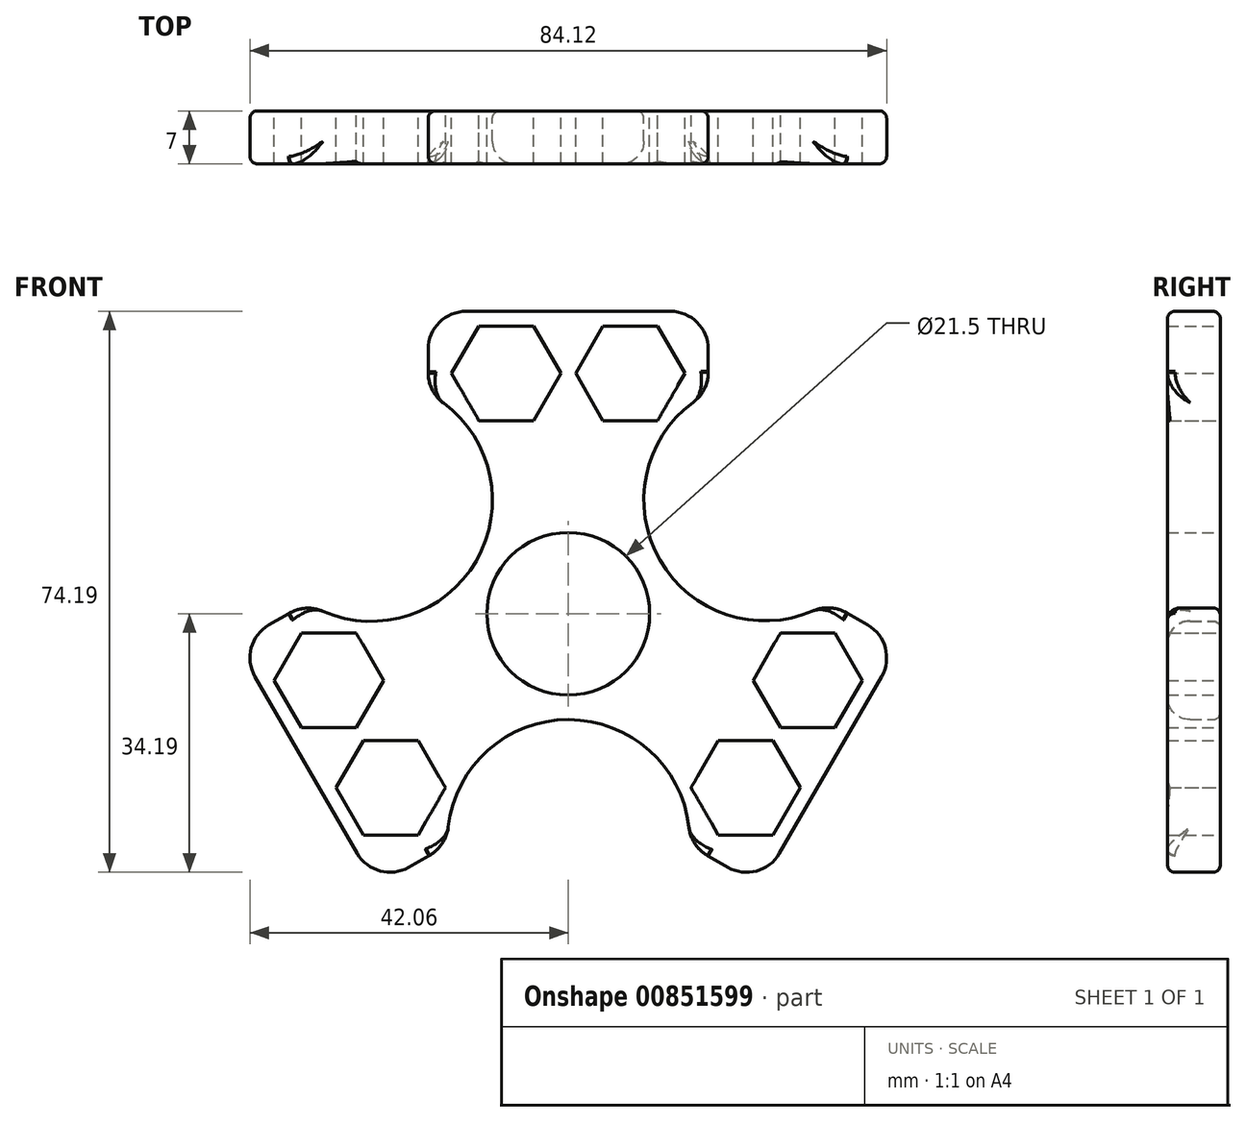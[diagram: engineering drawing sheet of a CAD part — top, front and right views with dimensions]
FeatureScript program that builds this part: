
annotation { "Feature Type Name" : "Feature", "Feature Type Description" : "" }
export const myFeature = defineFeature(function(context is Context, id is Id, definition is map)
    precondition{}
    {
        {
            var Q0;
            Q0=qCreatedBy(makeId("Front.planeOp"),FACE);
            var sketch = newSketch(context, id + "F0", { "sketchPlane" : qUnion([Q0])});
            skLineSegment(sketch, "E0", {"start": v(-11.55, 20) * mm, "end": v(-23.1, 0) * mm});
            skLineSegment(sketch, "E1", {"start": v(-11.55, -20) * mm, "end": v(11.55, -20) * mm});
            skLineSegment(sketch, "E2", {"start": v(23.1, 0) * mm, "end": v(11.55, 20) * mm});
            skLineSegment(sketch, "E3", {"start": v(-34.64, -20) * mm, "end": v(17.32, 10) * mm, "construction": true});
            skLineSegment(sketch, "E4", {"start": v(-17.32, 10) * mm, "end": v(34.64, -20) * mm, "construction": true});
            skLineSegment(sketch, "E5", {"start": v(0, -20) * mm, "end": v(0, 40) * mm, "construction": true});
            skLineSegment(sketch, "E6.bottom", {"start": v(18.5, 40) * mm, "end": v(-18.5, 40) * mm});
            skLineSegment(sketch, "E6.top", {"start": v(18.5, 20) * mm, "end": v(11.55, 20) * mm});
            skLineSegment(sketch, "E6.left", {"start": v(18.5, 40) * mm, "end": v(18.5, 20) * mm});
            skLineSegment(sketch, "E6.right", {"start": v(-18.5, 40) * mm, "end": v(-18.5, 20) * mm});
            skLineSegment(sketch, "E7", {"start": v(-43.9, -3.98) * mm, "end": v(-25.4, -36.02) * mm});
            skLineSegment(sketch, "E8", {"start": v(-25.4, -36.02) * mm, "end": v(-8.07, -26.02) * mm});
            skLineSegment(sketch, "E9", {"start": v(-8.07, -26.02) * mm, "end": v(-11.55, -20) * mm});
            skLineSegment(sketch, "E10", {"start": v(-26.57, 6.02) * mm, "end": v(-43.9, -3.98) * mm});
            skLineSegment(sketch, "E11", {"start": v(43.9, -3.98) * mm, "end": v(25.4, -36.02) * mm});
            skLineSegment(sketch, "E12", {"start": v(43.9, -3.98) * mm, "end": v(26.57, 6.02) * mm});
            skLineSegment(sketch, "E13", {"start": v(26.57, 6.02) * mm, "end": v(23.1, 0) * mm});
            skLineSegment(sketch, "E14", {"start": v(8.07, -26.02) * mm, "end": v(25.4, -36.02) * mm});
            skPoint(sketch, "E15.startSnap0", {"position": v(-35.23, 1.02) * mm});
            skLineSegment(sketch, "E16.trimOffspring", {"start": v(-23.1, 0) * mm, "end": v(-26.57, 6.02) * mm});
            skLineSegment(sketch, "E17.trimOffspring", {"start": v(11.55, -20) * mm, "end": v(8.07, -26.02) * mm});
            skLineSegment(sketch, "E18.trimOffspring", {"start": v(-11.55, 20) * mm, "end": v(-18.5, 20) * mm});
            skSolve(sketch);
        }
        {
            var Q0;
            Q0=makeQuery(id+"F0.imprint","IMPRINT",FACE,{"disambiguationData":[TD([[makeQuery(id+"F0.imprint","IMPRINT",EDGE,{"derivedFrom":sQuery(id+"F0.wireOp",EDGE,"E0")}),1.0]])]});
            extrude(context, id + "F1", {"entities" : qUnion([Q0]), "depth" : 7 * mm, "offsetDistance" : 25 * mm});
        }
        {
            var Q0;
            Q0=makeQuery(id+"F1.opExtrude","CAP_FACE",FACE,{"disambiguationData":[OSD([sQuery(id+"F0.wireOp",EDGE,"E0"),sQuery(id+"F0.wireOp",EDGE,"E1"),sQuery(id+"F0.wireOp",EDGE,"E2"),sQuery(id+"F0.wireOp",EDGE,"E6.bottom"),sQuery(id+"F0.wireOp",EDGE,"E6.top"),sQuery(id+"F0.wireOp",EDGE,"E6.left"),sQuery(id+"F0.wireOp",EDGE,"E6.right"),sQuery(id+"F0.wireOp",EDGE,"E7"),sQuery(id+"F0.wireOp",EDGE,"E8"),sQuery(id+"F0.wireOp",EDGE,"E9"),sQuery(id+"F0.wireOp",EDGE,"E10"),sQuery(id+"F0.wireOp",EDGE,"E11"),sQuery(id+"F0.wireOp",EDGE,"E12"),sQuery(id+"F0.wireOp",EDGE,"E13"),sQuery(id+"F0.wireOp",EDGE,"E14"),sQuery(id+"F0.wireOp",EDGE,"E16.trimOffspring"),sQuery(id+"F0.wireOp",EDGE,"E17.trimOffspring"),sQuery(id+"F0.wireOp",EDGE,"E18.trimOffspring")])],"isStart":true});
            var sketch = newSketch(context, id + "F2", { "sketchPlane" : qUnion([Q0])});
            skPoint(sketch, "E19.0", {"position": v(18.5, 30) * mm});
            skPoint(sketch, "E20.0", {"position": v(-18.5, 30) * mm});
            skPoint(sketch, "E21.0", {"position": v(-35.23, 1.02) * mm});
            skPoint(sketch, "E22.0", {"position": v(-16.73, -31.02) * mm});
            skPoint(sketch, "E23.0", {"position": v(16.73, -31.02) * mm});
            skPoint(sketch, "E24.0", {"position": v(35.23, 1.02) * mm});
            skLineSegment(sketch, "E25", {"start": v(-25.98, 15.07) * mm, "end": v(-9.98, 15.05) * mm});
            skLineSegment(sketch, "E26", {"start": v(-0.04, -30) * mm, "end": v(7.98, -16.15) * mm});
            skLineSegment(sketch, "E27", {"start": v(-0.04, -30) * mm, "end": v(-8.02, -16.13) * mm});
            skCircle(sketch, "E28", {"center": v(-25.98, 15.07) * mm, "radius": 16 * mm});
            skCircle(sketch, "E29", {"center": v(26.02, 15) * mm, "radius": 16 * mm});
            skCircle(sketch, "E30", {"center": v(-0.04, -30) * mm, "radius": 16 * mm});
            skLineSegment(sketch, "E31.trimOffspring", {"start": v(10.02, 15.02) * mm, "end": v(26.02, 15) * mm});
            skLineSegment(sketch, "E32.trimOffspring", {"start": v(-18, 1.2) * mm, "end": v(-25.98, 15.07) * mm});
            skLineSegment(sketch, "E33.trimOffspring", {"start": v(18, 1.15) * mm, "end": v(26.02, 15) * mm});
            skSolve(sketch);
        }
        {
            var Q0;
            Q0 = qSketchRegion(id + "F2", true);
            extrude(context, id + "F3", {"entities" : qUnion([Q0]), "operationType" : NewBodyOperationType.REMOVE, "oppositeDirection" : true, "depth" : 25 * mm, "offsetDistance" : 25 * mm});
        }
        {
            var Q0;
            Q0 = qSketchRegion(id + "F2", true);
            extrude(context, id + "F4", {"entities" : qUnion([Q0]), "operationType" : NewBodyOperationType.REMOVE, "oppositeDirection" : true, "depth" : 25 * mm, "offsetDistance" : 25 * mm});
        }
        {
            var Q0;
            Q0=makeQuery(id+"F3.boolean.opBoolean","INTERSECT",EDGE,{"derivedFrom":[makeQuery(id+"F1.opExtrude","SWEPT_FACE",FACE,{"disambiguationData":[OSD([sQuery(id+"F0.wireOp",EDGE,"E6.left")])]}),makeQuery(id+"F3.opExtrude","SWEPT_FACE",FACE,{"disambiguationData":[OSD([sQuery(id+"F2.wireOp",EDGE,"E28")])]})]});
            var Q1;
            Q1=makeQuery(id+"F3.boolean.opBoolean","INTERSECT",EDGE,{"derivedFrom":[makeQuery(id+"F1.opExtrude","SWEPT_FACE",FACE,{"disambiguationData":[OSD([sQuery(id+"F0.wireOp",EDGE,"E6.right")])]}),makeQuery(id+"F3.opExtrude","SWEPT_FACE",FACE,{"disambiguationData":[OSD([sQuery(id+"F2.wireOp",EDGE,"E29")])]})]});
            var Q2;
            Q2=makeQuery(id+"F3.boolean.opBoolean","INTERSECT",EDGE,{"derivedFrom":[makeQuery(id+"F1.opExtrude","SWEPT_FACE",FACE,{"disambiguationData":[OSD([sQuery(id+"F0.wireOp",EDGE,"E10")])]}),makeQuery(id+"F3.opExtrude","SWEPT_FACE",FACE,{"disambiguationData":[OSD([sQuery(id+"F2.wireOp",EDGE,"E29")])]})]});
            var Q3;
            Q3=makeQuery(id+"F3.boolean.opBoolean","INTERSECT",EDGE,{"derivedFrom":[makeQuery(id+"F1.opExtrude","SWEPT_FACE",FACE,{"disambiguationData":[OSD([sQuery(id+"F0.wireOp",EDGE,"E8")])]}),makeQuery(id+"F3.opExtrude","SWEPT_FACE",FACE,{"disambiguationData":[OSD([sQuery(id+"F2.wireOp",EDGE,"E30")])]})]});
            var Q4;
            Q4=makeQuery(id+"F3.boolean.opBoolean","INTERSECT",EDGE,{"derivedFrom":[makeQuery(id+"F1.opExtrude","SWEPT_FACE",FACE,{"disambiguationData":[OSD([sQuery(id+"F0.wireOp",EDGE,"E12")])]}),makeQuery(id+"F3.opExtrude","SWEPT_FACE",FACE,{"disambiguationData":[OSD([sQuery(id+"F2.wireOp",EDGE,"E28")])]})]});
            var Q5;
            Q5=makeQuery(id+"F3.boolean.opBoolean","INTERSECT",EDGE,{"derivedFrom":[makeQuery(id+"F1.opExtrude","SWEPT_FACE",FACE,{"disambiguationData":[OSD([sQuery(id+"F0.wireOp",EDGE,"E14")])]}),makeQuery(id+"F3.opExtrude","SWEPT_FACE",FACE,{"disambiguationData":[OSD([sQuery(id+"F2.wireOp",EDGE,"E30")])]})]});
            fillet(context, id + "F5", {"entities" : qUnion([Q0, Q1, Q2, Q3, Q4, Q5]), "radius" : 5 * mm, "tangentPropagation" : true, "allowEdgeOverflow" : false});
        }
        {
            var Q0;
            Q0=makeQuery(id+"F1.opExtrude","SWEPT_EDGE",EDGE,{"disambiguationData":[OSD([sQuery(id+"F0.wireOp",EDGE,"E7"),sQuery(id+"F0.wireOp",EDGE,"E8")])]});
            var Q1;
            Q1=makeQuery(id+"F1.opExtrude","SWEPT_EDGE",EDGE,{"disambiguationData":[OSD([sQuery(id+"F0.wireOp",EDGE,"E7"),sQuery(id+"F0.wireOp",EDGE,"E10")])]});
            var Q2;
            Q2=makeQuery(id+"F1.opExtrude","SWEPT_EDGE",EDGE,{"disambiguationData":[OSD([sQuery(id+"F0.wireOp",EDGE,"E6.bottom"),sQuery(id+"F0.wireOp",EDGE,"E6.right")])]});
            var Q3;
            Q3=makeQuery(id+"F1.opExtrude","SWEPT_EDGE",EDGE,{"disambiguationData":[OSD([sQuery(id+"F0.wireOp",EDGE,"E6.bottom"),sQuery(id+"F0.wireOp",EDGE,"E6.left")])]});
            var Q4;
            Q4=makeQuery(id+"F1.opExtrude","SWEPT_EDGE",EDGE,{"disambiguationData":[OSD([sQuery(id+"F0.wireOp",EDGE,"E11"),sQuery(id+"F0.wireOp",EDGE,"E12")])]});
            var Q5;
            Q5=makeQuery(id+"F1.opExtrude","SWEPT_EDGE",EDGE,{"disambiguationData":[OSD([sQuery(id+"F0.wireOp",EDGE,"E11"),sQuery(id+"F0.wireOp",EDGE,"E14")])]});
            fillet(context, id + "F6", {"entities" : qUnion([Q0, Q1, Q2, Q3, Q4, Q5]), "radius" : 5 * mm, "tangentPropagation" : true, "allowEdgeOverflow" : false});
        }
        {
            var Q0;
            Q0=makeQuery(id+"F1.opExtrude","CAP_FACE",FACE,{"disambiguationData":[OSD([sQuery(id+"F0.wireOp",EDGE,"E0"),sQuery(id+"F0.wireOp",EDGE,"E1"),sQuery(id+"F0.wireOp",EDGE,"E2"),sQuery(id+"F0.wireOp",EDGE,"E6.bottom"),sQuery(id+"F0.wireOp",EDGE,"E6.top"),sQuery(id+"F0.wireOp",EDGE,"E6.left"),sQuery(id+"F0.wireOp",EDGE,"E6.right"),sQuery(id+"F0.wireOp",EDGE,"E7"),sQuery(id+"F0.wireOp",EDGE,"E8"),sQuery(id+"F0.wireOp",EDGE,"E9"),sQuery(id+"F0.wireOp",EDGE,"E10"),sQuery(id+"F0.wireOp",EDGE,"E11"),sQuery(id+"F0.wireOp",EDGE,"E12"),sQuery(id+"F0.wireOp",EDGE,"E13"),sQuery(id+"F0.wireOp",EDGE,"E14"),sQuery(id+"F0.wireOp",EDGE,"E16.trimOffspring"),sQuery(id+"F0.wireOp",EDGE,"E17.trimOffspring"),sQuery(id+"F0.wireOp",EDGE,"E18.trimOffspring")])],"isStart":true});
            var sketch = newSketch(context, id + "F7", { "sketchPlane" : qUnion([Q0])});
            skLineSegment(sketch, "E34", {"start": v(0, 0) * mm, "end": v(34.64, -20) * mm, "construction": true});
            skLineSegment(sketch, "E35", {"start": v(-34.64, -20) * mm, "end": v(0, 0) * mm, "construction": true});
            skLineSegment(sketch, "E36", {"start": v(0, 40) * mm, "end": v(0, 0) * mm, "construction": true});
            skCircle(sketch, "E37.cCircle", {"center": v(31.64, -8.8) * mm, "radius": 6.25 * mm, "construction": true});
            skLineSegment(sketch, "E37.0", {"start": v(35.25, -2.55) * mm, "end": v(38.86, -8.8) * mm});
            skLineSegment(sketch, "E37.1", {"start": v(38.86, -8.8) * mm, "end": v(35.25, -15.05) * mm});
            skLineSegment(sketch, "E37.2", {"start": v(35.25, -15.05) * mm, "end": v(28.03, -15.05) * mm});
            skLineSegment(sketch, "E37.3", {"start": v(28.03, -15.05) * mm, "end": v(24.42, -8.8) * mm});
            skLineSegment(sketch, "E37.4", {"start": v(24.42, -8.8) * mm, "end": v(28.03, -2.55) * mm});
            skLineSegment(sketch, "E37.5", {"start": v(28.03, -2.55) * mm, "end": v(35.25, -2.55) * mm});
            skPoint(sketch, "E37.0.midPoint", {"position": v(37.05, -5.67) * mm});
            skCircle(sketch, "E38.cCircle", {"center": v(23.44, -23) * mm, "radius": 6.25 * mm, "construction": true});
            skLineSegment(sketch, "E38.0", {"start": v(27.05, -29.25) * mm, "end": v(19.83, -29.25) * mm});
            skLineSegment(sketch, "E38.1", {"start": v(19.83, -29.25) * mm, "end": v(16.22, -23) * mm});
            skLineSegment(sketch, "E38.2", {"start": v(16.22, -23) * mm, "end": v(19.83, -16.75) * mm});
            skLineSegment(sketch, "E38.3", {"start": v(19.83, -16.75) * mm, "end": v(27.05, -16.75) * mm});
            skLineSegment(sketch, "E38.4", {"start": v(27.05, -16.75) * mm, "end": v(30.66, -23) * mm});
            skLineSegment(sketch, "E38.5", {"start": v(30.66, -23) * mm, "end": v(27.05, -29.25) * mm});
            skPoint(sketch, "E38.0.midPoint", {"position": v(23.44, -29.25) * mm});
            skLineSegment(sketch, "E39.1.0", {"start": v(-4.6, 25.55) * mm, "end": v(-11.8, 25.55) * mm});
            skCircle(sketch, "E39.1.1", {"center": v(-8.2, 31.8) * mm, "radius": 6.25 * mm, "construction": true});
            skLineSegment(sketch, "E39.1.2", {"start": v(-11.8, 25.55) * mm, "end": v(-15.42, 31.8) * mm});
            skLineSegment(sketch, "E39.1.3", {"start": v(-15.42, 31.8) * mm, "end": v(-11.8, 38.05) * mm});
            skLineSegment(sketch, "E39.1.4", {"start": v(-11.8, 38.05) * mm, "end": v(-4.6, 38.05) * mm});
            skLineSegment(sketch, "E39.1.5", {"start": v(-4.6, 38.05) * mm, "end": v(-0.98, 31.8) * mm});
            skLineSegment(sketch, "E39.1.6", {"start": v(-0.98, 31.8) * mm, "end": v(-4.6, 25.55) * mm});
            skLineSegment(sketch, "E39.1.7", {"start": v(4.6, 25.55) * mm, "end": v(0.98, 31.8) * mm});
            skLineSegment(sketch, "E39.1.8", {"start": v(11.8, 25.55) * mm, "end": v(4.6, 25.55) * mm});
            skCircle(sketch, "E39.1.9", {"center": v(8.2, 31.8) * mm, "radius": 6.25 * mm, "construction": true});
            skLineSegment(sketch, "E39.1.10", {"start": v(0.98, 31.8) * mm, "end": v(4.6, 38.05) * mm});
            skLineSegment(sketch, "E39.1.11", {"start": v(4.6, 38.05) * mm, "end": v(11.8, 38.05) * mm});
            skLineSegment(sketch, "E39.1.12", {"start": v(11.8, 38.05) * mm, "end": v(15.42, 31.8) * mm});
            skLineSegment(sketch, "E39.1.13", {"start": v(15.42, 31.8) * mm, "end": v(11.8, 25.55) * mm});
            skLineSegment(sketch, "E39.2.0", {"start": v(-19.83, -16.75) * mm, "end": v(-16.22, -23) * mm});
            skCircle(sketch, "E39.2.1", {"center": v(-23.44, -23) * mm, "radius": 6.25 * mm, "construction": true});
            skLineSegment(sketch, "E39.2.2", {"start": v(-16.22, -23) * mm, "end": v(-19.83, -29.25) * mm});
            skLineSegment(sketch, "E39.2.3", {"start": v(-19.83, -29.25) * mm, "end": v(-27.05, -29.25) * mm});
            skLineSegment(sketch, "E39.2.4", {"start": v(-27.05, -29.25) * mm, "end": v(-30.66, -23) * mm});
            skLineSegment(sketch, "E39.2.5", {"start": v(-30.66, -23) * mm, "end": v(-27.05, -16.75) * mm});
            skLineSegment(sketch, "E39.2.6", {"start": v(-27.05, -16.75) * mm, "end": v(-19.83, -16.75) * mm});
            skLineSegment(sketch, "E39.2.7", {"start": v(-24.42, -8.8) * mm, "end": v(-28.03, -15.05) * mm});
            skLineSegment(sketch, "E39.2.8", {"start": v(-28.03, -2.55) * mm, "end": v(-24.42, -8.8) * mm});
            skCircle(sketch, "E39.2.9", {"center": v(-31.64, -8.8) * mm, "radius": 6.25 * mm, "construction": true});
            skLineSegment(sketch, "E39.2.10", {"start": v(-28.03, -15.05) * mm, "end": v(-35.25, -15.05) * mm});
            skLineSegment(sketch, "E39.2.11", {"start": v(-35.25, -15.05) * mm, "end": v(-38.86, -8.8) * mm});
            skLineSegment(sketch, "E39.2.12", {"start": v(-38.86, -8.8) * mm, "end": v(-35.25, -2.55) * mm});
            skLineSegment(sketch, "E39.2.13", {"start": v(-35.25, -2.55) * mm, "end": v(-28.03, -2.55) * mm});
            skPoint(sketch, "E39.center", {"position": v(0, 0) * mm});
            skSolve(sketch);
        }
        {
            var Q0;
            Q0 = qSketchRegion(id + "F7", true);
            extrude(context, id + "F8", {"entities" : qUnion([Q0]), "operationType" : NewBodyOperationType.REMOVE, "oppositeDirection" : true, "depth" : 25 * mm, "offsetDistance" : 25 * mm});
        }
        {
            var Q0;
            Q0=makeQuery(id+"F3.boolean.opBoolean","INTERSECT",EDGE,{"derivedFrom":[makeQuery(id+"F1.opExtrude","CAP_FACE",FACE,{"disambiguationData":[OSD([sQuery(id+"F0.wireOp",EDGE,"E0"),sQuery(id+"F0.wireOp",EDGE,"E1"),sQuery(id+"F0.wireOp",EDGE,"E2"),sQuery(id+"F0.wireOp",EDGE,"E6.bottom"),sQuery(id+"F0.wireOp",EDGE,"E6.top"),sQuery(id+"F0.wireOp",EDGE,"E6.left"),sQuery(id+"F0.wireOp",EDGE,"E6.right"),sQuery(id+"F0.wireOp",EDGE,"E7"),sQuery(id+"F0.wireOp",EDGE,"E8"),sQuery(id+"F0.wireOp",EDGE,"E9"),sQuery(id+"F0.wireOp",EDGE,"E10"),sQuery(id+"F0.wireOp",EDGE,"E11"),sQuery(id+"F0.wireOp",EDGE,"E12"),sQuery(id+"F0.wireOp",EDGE,"E13"),sQuery(id+"F0.wireOp",EDGE,"E14"),sQuery(id+"F0.wireOp",EDGE,"E16.trimOffspring"),sQuery(id+"F0.wireOp",EDGE,"E17.trimOffspring"),sQuery(id+"F0.wireOp",EDGE,"E18.trimOffspring")])],"isStart":false}),makeQuery(id+"F3.opExtrude","SWEPT_FACE",FACE,{"disambiguationData":[OSD([sQuery(id+"F2.wireOp",EDGE,"E29")])]})]});
            var Q1;
            Q1=makeQuery(id+"F3.boolean.opBoolean","COPY",EDGE,{"derivedFrom":makeQuery(id+"F3.opExtrude","CAP_EDGE",EDGE,{"disambiguationData":[OSD([sQuery(id+"F2.wireOp",EDGE,"E29")])],"isStart":true})});
            var Q2;
            Q2=makeQuery(id+"F3.boolean.opBoolean","INTERSECT",EDGE,{"derivedFrom":[makeQuery(id+"F1.opExtrude","CAP_FACE",FACE,{"disambiguationData":[OSD([sQuery(id+"F0.wireOp",EDGE,"E0"),sQuery(id+"F0.wireOp",EDGE,"E1"),sQuery(id+"F0.wireOp",EDGE,"E2"),sQuery(id+"F0.wireOp",EDGE,"E6.bottom"),sQuery(id+"F0.wireOp",EDGE,"E6.top"),sQuery(id+"F0.wireOp",EDGE,"E6.left"),sQuery(id+"F0.wireOp",EDGE,"E6.right"),sQuery(id+"F0.wireOp",EDGE,"E7"),sQuery(id+"F0.wireOp",EDGE,"E8"),sQuery(id+"F0.wireOp",EDGE,"E9"),sQuery(id+"F0.wireOp",EDGE,"E10"),sQuery(id+"F0.wireOp",EDGE,"E11"),sQuery(id+"F0.wireOp",EDGE,"E12"),sQuery(id+"F0.wireOp",EDGE,"E13"),sQuery(id+"F0.wireOp",EDGE,"E14"),sQuery(id+"F0.wireOp",EDGE,"E16.trimOffspring"),sQuery(id+"F0.wireOp",EDGE,"E17.trimOffspring"),sQuery(id+"F0.wireOp",EDGE,"E18.trimOffspring")])],"isStart":false}),makeQuery(id+"F3.opExtrude","SWEPT_FACE",FACE,{"disambiguationData":[OSD([sQuery(id+"F2.wireOp",EDGE,"E30")])]})]});
            var Q3;
            Q3=makeQuery(id+"F3.boolean.opBoolean","INTERSECT",EDGE,{"derivedFrom":[makeQuery(id+"F1.opExtrude","CAP_FACE",FACE,{"disambiguationData":[OSD([sQuery(id+"F0.wireOp",EDGE,"E0"),sQuery(id+"F0.wireOp",EDGE,"E1"),sQuery(id+"F0.wireOp",EDGE,"E2"),sQuery(id+"F0.wireOp",EDGE,"E6.bottom"),sQuery(id+"F0.wireOp",EDGE,"E6.top"),sQuery(id+"F0.wireOp",EDGE,"E6.left"),sQuery(id+"F0.wireOp",EDGE,"E6.right"),sQuery(id+"F0.wireOp",EDGE,"E7"),sQuery(id+"F0.wireOp",EDGE,"E8"),sQuery(id+"F0.wireOp",EDGE,"E9"),sQuery(id+"F0.wireOp",EDGE,"E10"),sQuery(id+"F0.wireOp",EDGE,"E11"),sQuery(id+"F0.wireOp",EDGE,"E12"),sQuery(id+"F0.wireOp",EDGE,"E13"),sQuery(id+"F0.wireOp",EDGE,"E14"),sQuery(id+"F0.wireOp",EDGE,"E16.trimOffspring"),sQuery(id+"F0.wireOp",EDGE,"E17.trimOffspring"),sQuery(id+"F0.wireOp",EDGE,"E18.trimOffspring")])],"isStart":false}),makeQuery(id+"F3.opExtrude","SWEPT_FACE",FACE,{"disambiguationData":[OSD([sQuery(id+"F2.wireOp",EDGE,"E28")])]})]});
            var Q4;
            Q4=makeQuery(id+"F3.boolean.opBoolean","COPY",EDGE,{"derivedFrom":makeQuery(id+"F3.opExtrude","CAP_EDGE",EDGE,{"disambiguationData":[OSD([sQuery(id+"F2.wireOp",EDGE,"E28")])],"isStart":true})});
            var Q5;
            Q5=makeQuery(id+"F3.boolean.opBoolean","COPY",EDGE,{"derivedFrom":makeQuery(id+"F3.opExtrude","CAP_EDGE",EDGE,{"disambiguationData":[OSD([sQuery(id+"F2.wireOp",EDGE,"E30")])],"isStart":true})});
            fillet(context, id + "F9", {"entities" : qUnion([Q0, Q1, Q2, Q3, Q4, Q5]), "radius" : 3 * mm, "allowEdgeOverflow" : false});
        }
        {
            var Q0;
            Q0=makeQuery(id+"F1.opExtrude","CAP_FACE",FACE,{"disambiguationData":[OSD([sQuery(id+"F0.wireOp",EDGE,"E0"),sQuery(id+"F0.wireOp",EDGE,"E1"),sQuery(id+"F0.wireOp",EDGE,"E2"),sQuery(id+"F0.wireOp",EDGE,"E6.bottom"),sQuery(id+"F0.wireOp",EDGE,"E6.top"),sQuery(id+"F0.wireOp",EDGE,"E6.left"),sQuery(id+"F0.wireOp",EDGE,"E6.right"),sQuery(id+"F0.wireOp",EDGE,"E7"),sQuery(id+"F0.wireOp",EDGE,"E8"),sQuery(id+"F0.wireOp",EDGE,"E9"),sQuery(id+"F0.wireOp",EDGE,"E10"),sQuery(id+"F0.wireOp",EDGE,"E11"),sQuery(id+"F0.wireOp",EDGE,"E12"),sQuery(id+"F0.wireOp",EDGE,"E13"),sQuery(id+"F0.wireOp",EDGE,"E14"),sQuery(id+"F0.wireOp",EDGE,"E16.trimOffspring"),sQuery(id+"F0.wireOp",EDGE,"E17.trimOffspring"),sQuery(id+"F0.wireOp",EDGE,"E18.trimOffspring")])],"isStart":true});
            var sketch = newSketch(context, id + "F10", { "sketchPlane" : qUnion([Q0])});
            skCircle(sketch, "E40", {"center": v(0, 0) * mm, "radius": 10.75 * mm});
            skSolve(sketch);
        }
        {
            var Q0;
            Q0 = qSketchRegion(id + "F10", true);
            extrude(context, id + "F11", {"entities" : qUnion([Q0]), "operationType" : NewBodyOperationType.REMOVE, "oppositeDirection" : true, "depth" : 25 * mm, "offsetDistance" : 25 * mm});
        }
        {
            var Q0;
            {var subQ0=sQuery(id+"F0.wireOp",EDGE,"E6.left");var subQ1=sQuery(id+"F0.wireOp",EDGE,"E6.bottom");Q0=makeQuery(id+"F6.opFillet","BLEND_EDGE",EDGE,{"blendedFrom":[makeQuery(id+"F1.opExtrude","SWEPT_EDGE",EDGE,{"disambiguationData":[OSD([subQ1,subQ0])]}),makeQuery(id+"F1.opExtrude","CAP_FACE",FACE,{"disambiguationData":[OSD([sQuery(id+"F0.wireOp",EDGE,"E0"),sQuery(id+"F0.wireOp",EDGE,"E1"),sQuery(id+"F0.wireOp",EDGE,"E2"),subQ1,sQuery(id+"F0.wireOp",EDGE,"E6.top"),subQ0,sQuery(id+"F0.wireOp",EDGE,"E6.right"),sQuery(id+"F0.wireOp",EDGE,"E7"),sQuery(id+"F0.wireOp",EDGE,"E8"),sQuery(id+"F0.wireOp",EDGE,"E9"),sQuery(id+"F0.wireOp",EDGE,"E10"),sQuery(id+"F0.wireOp",EDGE,"E11"),sQuery(id+"F0.wireOp",EDGE,"E12"),sQuery(id+"F0.wireOp",EDGE,"E13"),sQuery(id+"F0.wireOp",EDGE,"E14"),sQuery(id+"F0.wireOp",EDGE,"E16.trimOffspring"),sQuery(id+"F0.wireOp",EDGE,"E17.trimOffspring"),sQuery(id+"F0.wireOp",EDGE,"E18.trimOffspring")])],"isStart":false})],"blendedInto":[makeQuery(id+"F1.opExtrude","CAP_FACE",FACE,{"disambiguationData":[OSD([sQuery(id+"F0.wireOp",EDGE,"E0"),sQuery(id+"F0.wireOp",EDGE,"E1"),sQuery(id+"F0.wireOp",EDGE,"E2"),subQ1,sQuery(id+"F0.wireOp",EDGE,"E6.top"),subQ0,sQuery(id+"F0.wireOp",EDGE,"E6.right"),sQuery(id+"F0.wireOp",EDGE,"E7"),sQuery(id+"F0.wireOp",EDGE,"E8"),sQuery(id+"F0.wireOp",EDGE,"E9"),sQuery(id+"F0.wireOp",EDGE,"E10"),sQuery(id+"F0.wireOp",EDGE,"E11"),sQuery(id+"F0.wireOp",EDGE,"E12"),sQuery(id+"F0.wireOp",EDGE,"E13"),sQuery(id+"F0.wireOp",EDGE,"E14"),sQuery(id+"F0.wireOp",EDGE,"E16.trimOffspring"),sQuery(id+"F0.wireOp",EDGE,"E17.trimOffspring"),sQuery(id+"F0.wireOp",EDGE,"E18.trimOffspring")])],"isStart":false})]});}
            var Q1;
            {var subQ0=sQuery(id+"F0.wireOp",EDGE,"E6.right");var subQ1=sQuery(id+"F0.wireOp",EDGE,"E6.bottom");Q1=makeQuery(id+"F6.opFillet","BLEND_EDGE",EDGE,{"blendedFrom":[makeQuery(id+"F1.opExtrude","SWEPT_EDGE",EDGE,{"disambiguationData":[OSD([subQ1,subQ0])]}),makeQuery(id+"F1.opExtrude","CAP_FACE",FACE,{"disambiguationData":[OSD([sQuery(id+"F0.wireOp",EDGE,"E0"),sQuery(id+"F0.wireOp",EDGE,"E1"),sQuery(id+"F0.wireOp",EDGE,"E2"),subQ1,sQuery(id+"F0.wireOp",EDGE,"E6.top"),sQuery(id+"F0.wireOp",EDGE,"E6.left"),subQ0,sQuery(id+"F0.wireOp",EDGE,"E7"),sQuery(id+"F0.wireOp",EDGE,"E8"),sQuery(id+"F0.wireOp",EDGE,"E9"),sQuery(id+"F0.wireOp",EDGE,"E10"),sQuery(id+"F0.wireOp",EDGE,"E11"),sQuery(id+"F0.wireOp",EDGE,"E12"),sQuery(id+"F0.wireOp",EDGE,"E13"),sQuery(id+"F0.wireOp",EDGE,"E14"),sQuery(id+"F0.wireOp",EDGE,"E16.trimOffspring"),sQuery(id+"F0.wireOp",EDGE,"E17.trimOffspring"),sQuery(id+"F0.wireOp",EDGE,"E18.trimOffspring")])],"isStart":true})],"blendedInto":[makeQuery(id+"F1.opExtrude","CAP_FACE",FACE,{"disambiguationData":[OSD([sQuery(id+"F0.wireOp",EDGE,"E0"),sQuery(id+"F0.wireOp",EDGE,"E1"),sQuery(id+"F0.wireOp",EDGE,"E2"),subQ1,sQuery(id+"F0.wireOp",EDGE,"E6.top"),sQuery(id+"F0.wireOp",EDGE,"E6.left"),subQ0,sQuery(id+"F0.wireOp",EDGE,"E7"),sQuery(id+"F0.wireOp",EDGE,"E8"),sQuery(id+"F0.wireOp",EDGE,"E9"),sQuery(id+"F0.wireOp",EDGE,"E10"),sQuery(id+"F0.wireOp",EDGE,"E11"),sQuery(id+"F0.wireOp",EDGE,"E12"),sQuery(id+"F0.wireOp",EDGE,"E13"),sQuery(id+"F0.wireOp",EDGE,"E14"),sQuery(id+"F0.wireOp",EDGE,"E16.trimOffspring"),sQuery(id+"F0.wireOp",EDGE,"E17.trimOffspring"),sQuery(id+"F0.wireOp",EDGE,"E18.trimOffspring")])],"isStart":true})]});}
            var Q2;
            {var subQ0=sQuery(id+"F0.wireOp",EDGE,"E10");var subQ1=sQuery(id+"F0.wireOp",EDGE,"E7");Q2=makeQuery(id+"F6.opFillet","BLEND_EDGE",EDGE,{"blendedFrom":[makeQuery(id+"F1.opExtrude","SWEPT_EDGE",EDGE,{"disambiguationData":[OSD([subQ1,subQ0])]}),makeQuery(id+"F1.opExtrude","CAP_FACE",FACE,{"disambiguationData":[OSD([sQuery(id+"F0.wireOp",EDGE,"E0"),sQuery(id+"F0.wireOp",EDGE,"E1"),sQuery(id+"F0.wireOp",EDGE,"E2"),sQuery(id+"F0.wireOp",EDGE,"E6.bottom"),sQuery(id+"F0.wireOp",EDGE,"E6.top"),sQuery(id+"F0.wireOp",EDGE,"E6.left"),sQuery(id+"F0.wireOp",EDGE,"E6.right"),subQ1,sQuery(id+"F0.wireOp",EDGE,"E8"),sQuery(id+"F0.wireOp",EDGE,"E9"),subQ0,sQuery(id+"F0.wireOp",EDGE,"E11"),sQuery(id+"F0.wireOp",EDGE,"E12"),sQuery(id+"F0.wireOp",EDGE,"E13"),sQuery(id+"F0.wireOp",EDGE,"E14"),sQuery(id+"F0.wireOp",EDGE,"E16.trimOffspring"),sQuery(id+"F0.wireOp",EDGE,"E17.trimOffspring"),sQuery(id+"F0.wireOp",EDGE,"E18.trimOffspring")])],"isStart":false})],"blendedInto":[makeQuery(id+"F1.opExtrude","CAP_FACE",FACE,{"disambiguationData":[OSD([sQuery(id+"F0.wireOp",EDGE,"E0"),sQuery(id+"F0.wireOp",EDGE,"E1"),sQuery(id+"F0.wireOp",EDGE,"E2"),sQuery(id+"F0.wireOp",EDGE,"E6.bottom"),sQuery(id+"F0.wireOp",EDGE,"E6.top"),sQuery(id+"F0.wireOp",EDGE,"E6.left"),sQuery(id+"F0.wireOp",EDGE,"E6.right"),subQ1,sQuery(id+"F0.wireOp",EDGE,"E8"),sQuery(id+"F0.wireOp",EDGE,"E9"),subQ0,sQuery(id+"F0.wireOp",EDGE,"E11"),sQuery(id+"F0.wireOp",EDGE,"E12"),sQuery(id+"F0.wireOp",EDGE,"E13"),sQuery(id+"F0.wireOp",EDGE,"E14"),sQuery(id+"F0.wireOp",EDGE,"E16.trimOffspring"),sQuery(id+"F0.wireOp",EDGE,"E17.trimOffspring"),sQuery(id+"F0.wireOp",EDGE,"E18.trimOffspring")])],"isStart":false})]});}
            var Q3;
            {var subQ0=sQuery(id+"F0.wireOp",EDGE,"E10");var subQ1=sQuery(id+"F0.wireOp",EDGE,"E7");Q3=makeQuery(id+"F6.opFillet","BLEND_EDGE",EDGE,{"blendedFrom":[makeQuery(id+"F1.opExtrude","SWEPT_EDGE",EDGE,{"disambiguationData":[OSD([subQ1,subQ0])]}),makeQuery(id+"F1.opExtrude","CAP_FACE",FACE,{"disambiguationData":[OSD([sQuery(id+"F0.wireOp",EDGE,"E0"),sQuery(id+"F0.wireOp",EDGE,"E1"),sQuery(id+"F0.wireOp",EDGE,"E2"),sQuery(id+"F0.wireOp",EDGE,"E6.bottom"),sQuery(id+"F0.wireOp",EDGE,"E6.top"),sQuery(id+"F0.wireOp",EDGE,"E6.left"),sQuery(id+"F0.wireOp",EDGE,"E6.right"),subQ1,sQuery(id+"F0.wireOp",EDGE,"E8"),sQuery(id+"F0.wireOp",EDGE,"E9"),subQ0,sQuery(id+"F0.wireOp",EDGE,"E11"),sQuery(id+"F0.wireOp",EDGE,"E12"),sQuery(id+"F0.wireOp",EDGE,"E13"),sQuery(id+"F0.wireOp",EDGE,"E14"),sQuery(id+"F0.wireOp",EDGE,"E16.trimOffspring"),sQuery(id+"F0.wireOp",EDGE,"E17.trimOffspring"),sQuery(id+"F0.wireOp",EDGE,"E18.trimOffspring")])],"isStart":true})],"blendedInto":[makeQuery(id+"F1.opExtrude","CAP_FACE",FACE,{"disambiguationData":[OSD([sQuery(id+"F0.wireOp",EDGE,"E0"),sQuery(id+"F0.wireOp",EDGE,"E1"),sQuery(id+"F0.wireOp",EDGE,"E2"),sQuery(id+"F0.wireOp",EDGE,"E6.bottom"),sQuery(id+"F0.wireOp",EDGE,"E6.top"),sQuery(id+"F0.wireOp",EDGE,"E6.left"),sQuery(id+"F0.wireOp",EDGE,"E6.right"),subQ1,sQuery(id+"F0.wireOp",EDGE,"E8"),sQuery(id+"F0.wireOp",EDGE,"E9"),subQ0,sQuery(id+"F0.wireOp",EDGE,"E11"),sQuery(id+"F0.wireOp",EDGE,"E12"),sQuery(id+"F0.wireOp",EDGE,"E13"),sQuery(id+"F0.wireOp",EDGE,"E14"),sQuery(id+"F0.wireOp",EDGE,"E16.trimOffspring"),sQuery(id+"F0.wireOp",EDGE,"E17.trimOffspring"),sQuery(id+"F0.wireOp",EDGE,"E18.trimOffspring")])],"isStart":true})]});}
            var Q4;
            {var subQ0=sQuery(id+"F0.wireOp",EDGE,"E12");var subQ1=sQuery(id+"F0.wireOp",EDGE,"E11");Q4=makeQuery(id+"F6.opFillet","BLEND_EDGE",EDGE,{"blendedFrom":[makeQuery(id+"F1.opExtrude","SWEPT_EDGE",EDGE,{"disambiguationData":[OSD([subQ1,subQ0])]}),makeQuery(id+"F1.opExtrude","CAP_FACE",FACE,{"disambiguationData":[OSD([sQuery(id+"F0.wireOp",EDGE,"E0"),sQuery(id+"F0.wireOp",EDGE,"E1"),sQuery(id+"F0.wireOp",EDGE,"E2"),sQuery(id+"F0.wireOp",EDGE,"E6.bottom"),sQuery(id+"F0.wireOp",EDGE,"E6.top"),sQuery(id+"F0.wireOp",EDGE,"E6.left"),sQuery(id+"F0.wireOp",EDGE,"E6.right"),sQuery(id+"F0.wireOp",EDGE,"E7"),sQuery(id+"F0.wireOp",EDGE,"E8"),sQuery(id+"F0.wireOp",EDGE,"E9"),sQuery(id+"F0.wireOp",EDGE,"E10"),subQ1,subQ0,sQuery(id+"F0.wireOp",EDGE,"E13"),sQuery(id+"F0.wireOp",EDGE,"E14"),sQuery(id+"F0.wireOp",EDGE,"E16.trimOffspring"),sQuery(id+"F0.wireOp",EDGE,"E17.trimOffspring"),sQuery(id+"F0.wireOp",EDGE,"E18.trimOffspring")])],"isStart":false})],"blendedInto":[makeQuery(id+"F1.opExtrude","CAP_FACE",FACE,{"disambiguationData":[OSD([sQuery(id+"F0.wireOp",EDGE,"E0"),sQuery(id+"F0.wireOp",EDGE,"E1"),sQuery(id+"F0.wireOp",EDGE,"E2"),sQuery(id+"F0.wireOp",EDGE,"E6.bottom"),sQuery(id+"F0.wireOp",EDGE,"E6.top"),sQuery(id+"F0.wireOp",EDGE,"E6.left"),sQuery(id+"F0.wireOp",EDGE,"E6.right"),sQuery(id+"F0.wireOp",EDGE,"E7"),sQuery(id+"F0.wireOp",EDGE,"E8"),sQuery(id+"F0.wireOp",EDGE,"E9"),sQuery(id+"F0.wireOp",EDGE,"E10"),subQ1,subQ0,sQuery(id+"F0.wireOp",EDGE,"E13"),sQuery(id+"F0.wireOp",EDGE,"E14"),sQuery(id+"F0.wireOp",EDGE,"E16.trimOffspring"),sQuery(id+"F0.wireOp",EDGE,"E17.trimOffspring"),sQuery(id+"F0.wireOp",EDGE,"E18.trimOffspring")])],"isStart":false})]});}
            var Q5;
            {var subQ0=sQuery(id+"F0.wireOp",EDGE,"E12");var subQ1=sQuery(id+"F0.wireOp",EDGE,"E11");Q5=makeQuery(id+"F6.opFillet","BLEND_EDGE",EDGE,{"blendedFrom":[makeQuery(id+"F1.opExtrude","SWEPT_EDGE",EDGE,{"disambiguationData":[OSD([subQ1,subQ0])]}),makeQuery(id+"F1.opExtrude","CAP_FACE",FACE,{"disambiguationData":[OSD([sQuery(id+"F0.wireOp",EDGE,"E0"),sQuery(id+"F0.wireOp",EDGE,"E1"),sQuery(id+"F0.wireOp",EDGE,"E2"),sQuery(id+"F0.wireOp",EDGE,"E6.bottom"),sQuery(id+"F0.wireOp",EDGE,"E6.top"),sQuery(id+"F0.wireOp",EDGE,"E6.left"),sQuery(id+"F0.wireOp",EDGE,"E6.right"),sQuery(id+"F0.wireOp",EDGE,"E7"),sQuery(id+"F0.wireOp",EDGE,"E8"),sQuery(id+"F0.wireOp",EDGE,"E9"),sQuery(id+"F0.wireOp",EDGE,"E10"),subQ1,subQ0,sQuery(id+"F0.wireOp",EDGE,"E13"),sQuery(id+"F0.wireOp",EDGE,"E14"),sQuery(id+"F0.wireOp",EDGE,"E16.trimOffspring"),sQuery(id+"F0.wireOp",EDGE,"E17.trimOffspring"),sQuery(id+"F0.wireOp",EDGE,"E18.trimOffspring")])],"isStart":true})],"blendedInto":[makeQuery(id+"F1.opExtrude","CAP_FACE",FACE,{"disambiguationData":[OSD([sQuery(id+"F0.wireOp",EDGE,"E0"),sQuery(id+"F0.wireOp",EDGE,"E1"),sQuery(id+"F0.wireOp",EDGE,"E2"),sQuery(id+"F0.wireOp",EDGE,"E6.bottom"),sQuery(id+"F0.wireOp",EDGE,"E6.top"),sQuery(id+"F0.wireOp",EDGE,"E6.left"),sQuery(id+"F0.wireOp",EDGE,"E6.right"),sQuery(id+"F0.wireOp",EDGE,"E7"),sQuery(id+"F0.wireOp",EDGE,"E8"),sQuery(id+"F0.wireOp",EDGE,"E9"),sQuery(id+"F0.wireOp",EDGE,"E10"),subQ1,subQ0,sQuery(id+"F0.wireOp",EDGE,"E13"),sQuery(id+"F0.wireOp",EDGE,"E14"),sQuery(id+"F0.wireOp",EDGE,"E16.trimOffspring"),sQuery(id+"F0.wireOp",EDGE,"E17.trimOffspring"),sQuery(id+"F0.wireOp",EDGE,"E18.trimOffspring")])],"isStart":true})]});}
            fillet(context, id + "F12", {"entities" : qUnion([Q0, Q1, Q2, Q3, Q4, Q5]), "radius" : 1 * mm, "tangentPropagation" : true, "allowEdgeOverflow" : false});
        }
    });
